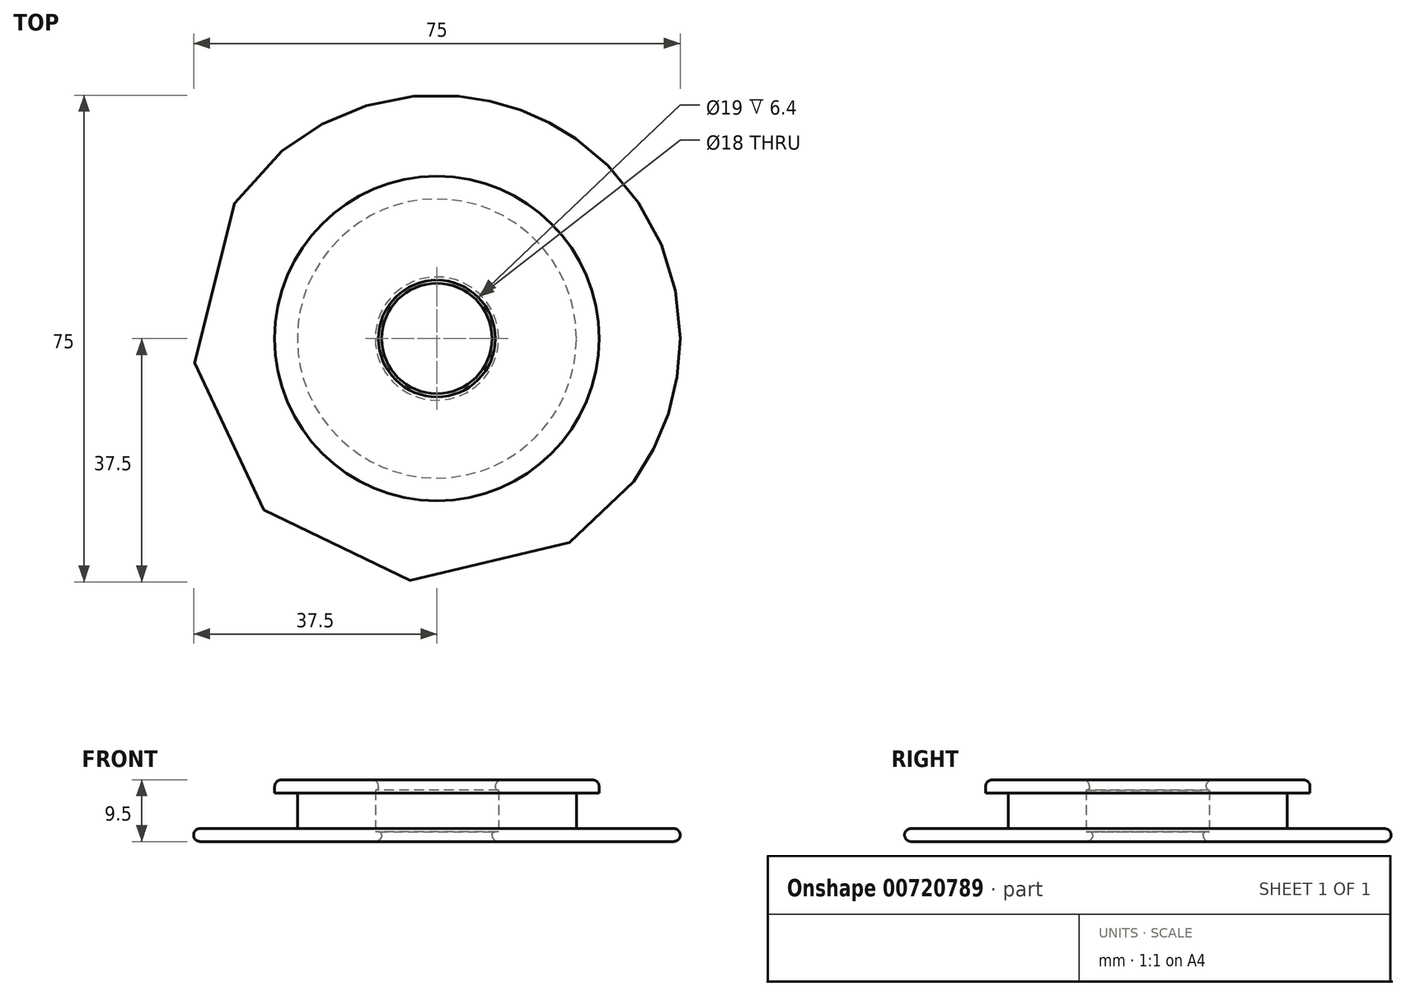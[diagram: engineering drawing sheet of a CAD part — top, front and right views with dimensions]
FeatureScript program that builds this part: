
annotation { "Feature Type Name" : "Feature", "Feature Type Description" : "" }
export const myFeature = defineFeature(function(context is Context, id is Id, definition is map)
    precondition{}
    {
        {
            var Q0;
            Q0=qCreatedBy(makeId("Top.planeOp"),FACE);
            var sketch = newSketch(context, id + "F0", { "sketchPlane" : qUnion([Q0])});
            skCircle(sketch, "E0", {"center": v(0, 0) * mm, "radius": 9.5 * mm});
            skCircle(sketch, "E1", {"center": v(0, 0) * mm, "radius": 25 * mm});
            skCircle(sketch, "E2", {"center": v(0, 0) * mm, "radius": 37.5 * mm});
            skSolve(sketch);
        }
        {
            var Q0;
            Q0=makeQuery(id+"F0.imprint","IMPRINT",FACE,{"disambiguationData":[TD([[makeQuery(id+"F0.imprint","IMPRINT",EDGE,{"derivedFrom":sQuery(id+"F0.wireOp",EDGE,"E0")}),-1.0]])]});
            extrude(context, id + "F1", {"entities" : qUnion([Q0]), "depth" : 9.5 * mm, "offsetDistance" : 25 * mm});
        }
        {
            var Q0;
            Q0=qCreatedBy(makeId("Right.planeOp"),FACE);
            var sketch = newSketch(context, id + "F2", { "sketchPlane" : qUnion([Q0])});
            skLineSegment(sketch, "E3", {"start": v(0, 0) * mm, "end": v(25, 0) * mm});
            skLineSegment(sketch, "E4", {"start": v(25, 0) * mm, "end": v(25, 11) * mm});
            skLineSegment(sketch, "E5", {"start": v(0, 0) * mm, "end": v(0, 26.52) * mm, "construction": true});
            skLineSegment(sketch, "E6", {"start": v(25, 0) * mm, "end": v(25, 2) * mm, "construction": true});
            skLineSegment(sketch, "E7.bottom", {"start": v(25, 2) * mm, "end": v(21.5, 2) * mm});
            skLineSegment(sketch, "E7.top", {"start": v(25, 7.5) * mm, "end": v(21.5, 7.5) * mm});
            skLineSegment(sketch, "E7.left", {"start": v(25, 2) * mm, "end": v(25, 7.5) * mm});
            skLineSegment(sketch, "E7.right", {"start": v(21.5, 2) * mm, "end": v(21.5, 7.5) * mm});
            skSolve(sketch);
        }
        {
            var Q0;
            Q0 = qSketchRegion(id + "F2", true);
            var Q1;
            Q1=sQuery(id+"F2.wireOp",EDGE,"E5");
            revolve(context, id + "F3", {"operationType" : NewBodyOperationType.REMOVE, "surfaceOperationType" : NewSurfaceOperationType.NEW, "entities" : qUnion([Q0]), "axis" : qUnion([Q1]), "revolveType" : RevolveType.FULL, "oppositeDirection" : true});
        }
        {
            var Q0;
            Q0=makeQuery(id+"F1.opExtrude","CAP_FACE",FACE,{"disambiguationData":[OSD([sQuery(id+"F0.wireOp",EDGE,"E0"),sQuery(id+"F0.wireOp",EDGE,"E1")])],"isStart":true});
            var sketch = newSketch(context, id + "F4", { "sketchPlane" : qUnion([Q0])});
            skCircle(sketch, "E8", {"center": v(0, 0) * mm, "radius": 8.5 * mm});
            skSolve(sketch);
        }
        {
            var Q0;
            Q0=makeQuery(id+"F4.imprint","IMPRINT",FACE,{"disambiguationData":[TD([[makeQuery(id+"F4.imprint","IMPRINT",EDGE,{"derivedFrom":sQuery(id+"F4.wireOp",EDGE,"E8")}),-1.0]])]});
            extrude(context, id + "F5", {"entities" : qUnion([Q0]), "operationType" : NewBodyOperationType.ADD, "oppositeDirection" : true, "depth" : 1.5 * mm, "offsetDistance" : 25 * mm});
        }
        {
            var Q0;
            Q0=makeQuery(id+"F1.opExtrude","CAP_FACE",FACE,{"disambiguationData":[OSD([sQuery(id+"F0.wireOp",EDGE,"E0"),sQuery(id+"F0.wireOp",EDGE,"E1")])],"isStart":false});
            var sketch = newSketch(context, id + "F6", { "sketchPlane" : qUnion([Q0])});
            skCircle(sketch, "E9", {"center": v(0, 0) * mm, "radius": 9 * mm});
            skSolve(sketch);
        }
        {
            var Q0;
            Q0=makeQuery(id+"F6.imprint","IMPRINT",FACE,{"disambiguationData":[TD([[makeQuery(id+"F6.imprint","IMPRINT",EDGE,{"derivedFrom":sQuery(id+"F6.wireOp",EDGE,"E9")}),-1.0]])]});
            extrude(context, id + "F7", {"entities" : qUnion([Q0]), "operationType" : NewBodyOperationType.ADD, "oppositeDirection" : true, "depth" : 1.6 * mm, "offsetDistance" : 25 * mm});
        }
        {
            var Q0;
            Q0=makeQuery(id+"F0.imprint","IMPRINT",FACE,{"disambiguationData":[TD([[makeQuery(id+"F0.imprint","IMPRINT",EDGE,{"derivedFrom":sQuery(id+"F0.wireOp",EDGE,"E1")}),-1.0]])]});
            extrude(context, id + "F8", {"entities" : qUnion([Q0]), "operationType" : NewBodyOperationType.ADD, "depth" : 2 * mm, "offsetDistance" : 25 * mm});
        }
        {
            var Q0;
            Q0=makeQuery(id+"F8.opExtrude","SWEPT_FACE",FACE,{"disambiguationData":[OSD([sQuery(id+"F0.wireOp",EDGE,"E2")])]});
            var Q1;
            {var subQ0=sQuery(id+"F0.wireOp",EDGE,"E0");Q1=makeQuery(id+"F7.boolean.opBoolean","MERGE",FACE,{"derivedFrom":[makeQuery(id+"F1.opExtrude","CAP_FACE",FACE,{"disambiguationData":[OSD([subQ0,sQuery(id+"F0.wireOp",EDGE,"E1")])],"isStart":false}),makeQuery(id+"F7.opExtrude","CAP_FACE",FACE,{"disambiguationData":[OSD([subQ0,sQuery(id+"F6.wireOp",EDGE,"E9")])],"isStart":true})]});}
            var Q2;
            Q2=makeQuery(id+"F5.opExtrude","CAP_EDGE",EDGE,{"disambiguationData":[OSD([sQuery(id+"F4.wireOp",EDGE,"E8")])],"isStart":true});
            fillet(context, id + "F9", {"entities" : qUnion([Q0, Q1, Q2]), "radius" : 1 * mm, "tangentPropagation" : true, "allowEdgeOverflow" : false});
        }
        {
            var Q0;
            Q0=makeQuery(id+"F5.opExtrude","CAP_EDGE",EDGE,{"disambiguationData":[OSD([sQuery(id+"F4.wireOp",EDGE,"E8")])],"isStart":false});
            var Q1;
            Q1=makeQuery(id+"F7.opExtrude","CAP_EDGE",EDGE,{"disambiguationData":[OSD([sQuery(id+"F6.wireOp",EDGE,"E9")])],"isStart":false});
            fillet(context, id + "F10", {"entities" : qUnion([Q0, Q1]), "radius" : .5 * mm, "tangentPropagation" : true, "allowEdgeOverflow" : false});
        }
    });
